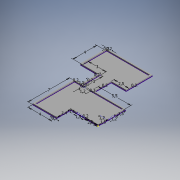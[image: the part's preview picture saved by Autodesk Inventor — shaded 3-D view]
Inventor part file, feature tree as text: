
AUTODESK INVENTOR PART (.ipt)
format: ipt  version: 2019.4 (Build 234330000, 330)  size: 168,960 bytes
history: native  units: mm (DEFAULTED — no unit token found)
features: extrude x2, sketch x1
ambient origin geometry x8: Origin, YZ Plane, XZ Plane, XY Plane, X Axis, Y Axis, Z Axis, Center Point
bodies: Solid1 (feature_tree)
feature tree (3):
  sketch  "Sketch1"  dims[d1=1500.0mm d2=2000.0mm d3=200.0mm d4=2200.0mm d5=1200.0mm d6=1500.0mm d7=5500.0mm d8=200.0mm d9=1200.0mm d10=1200.0mm d11=1500.0mm d12=1500.0mm d14=7000.0mm d15=4000.0mm d16=1100.0mm d17=2400.0mm d18=3000.0mm d19=3000.0mm d20=4000.0mm d22=300.0mm d23=200.0mm d25=200.0mm d27=200.0mm d29=300.0mm d30=200.0mm d32=200.0mm d33=200.0mm d34=200.0mm d35=2500.0mm d36=200.0mm d37=200.0mm d38=0.0mm d39=100.0mm d40=0.0mm]
  extrude  "Extrusion1"  Depth=2000.0mm
  extrude  "Extrusion2"  Depth=200.0mm
